# Revit family: Zumtobel MELLOW LIGHT 6 evo - AB
name_source: partatom
category: Lighting Fixtures
revit_build: Autodesk Revit 2014 (Build: 20140709_2115(x64)
units: mm (PartAtom-declared; Revit-internal decimal feet)

## types (6) — shared parameters
Assembly Code = D5020200
Body = Zumtobel_Metal_White
Color Filter = 16777215
Cover = Zumtobel_Metal_Aluminium
Description = Mellow light surface-mounted luminaire
Dimming Lamp Color Temperature Shift = <None>
Emit Shape Visible in Rendering = No
Height = 69 mm  [stored 0.226378 ft]
Lamp = LED
Manufacturer = Zumtobel Lighting
Tilt Angle = 90.00°
URL = http://www.zumtobel.com
42182682
Voltage = 230 V
Wings = Zumtobel_PMMA_White
zero-valued in all types: Default Elevation

## per-type parameters (varying)
| type | Apparent Load | Emit from Rectangle Length | Emit from Rectangle Width | Length | Middle Part | Model | Photometric Web File | Width |
| ML evo AA LED3600 Q | 30 VA | 555 mm | 537 mm  [stored 1.76181 ft] | 600 mm | Zumtobel_PMMA_White_Diffusor | 42185186 | D37832AA_MLevo_AA_LED3600-840_Q_complete.ies | 582 mm  [stored 1.90945 ft] |
| ML evo AL LED3600 Q | 29 VA | 555 mm | 537 mm  [stored 1.76181 ft] | 600 mm | Zumtobel_PMMA_White | 42184767 | D37836AA_MLevo_AL_LED3600-840_Q.ies | 582 mm  [stored 1.90945 ft] |
| ML evo AL LED3600 L | 29 VA | 1106 mm | 304 mm  [stored 0.997375 ft] | 1151 mm  [stored 3.77625 ft] | Zumtobel_PMMA_White | 42184766 | D37822AA_MLevo_AL_LED3600-840_L.ies | 349 mm  [stored 1.14501 ft] |
| ML evo AA LED4800 Q | 44 VA | 555 mm | 537 mm  [stored 1.76181 ft] | 600 mm | Zumtobel_PMMA_White_Diffusor | 42184764 | D37832AA_MLevo_AA_LED4800-840_Q_complete.ies | 582 mm  [stored 1.90945 ft] |
| ML evo AA LED4800 L | 44 VA | 1106 mm | 304 mm  [stored 0.997375 ft] | 1151 mm  [stored 3.77625 ft] | Zumtobel_PMMA_White_Diffusor | 42184763 | D37812AA_MLevo_AA_LED4800-840_L_complete.ies | 349 mm  [stored 1.14501 ft] |
| ML evo AA LED3600 L | 30 VA | 1106 mm | 304 mm  [stored 0.997375 ft] | 1151 mm  [stored 3.77625 ft] | Zumtobel_PMMA_White_Diffusor | 42185187 | D37812AA_MLevo_AA_LED3600-840_L_complete.ies | 349 mm  [stored 1.14501 ft] |

note: [stored X ft] marks values corroborated as IEEE doubles in the binary element streams (Revit-internal decimal feet)

## geometry (parser evidence)
native form markers: Sweep x3
no freeform markers — native parametric forms only
